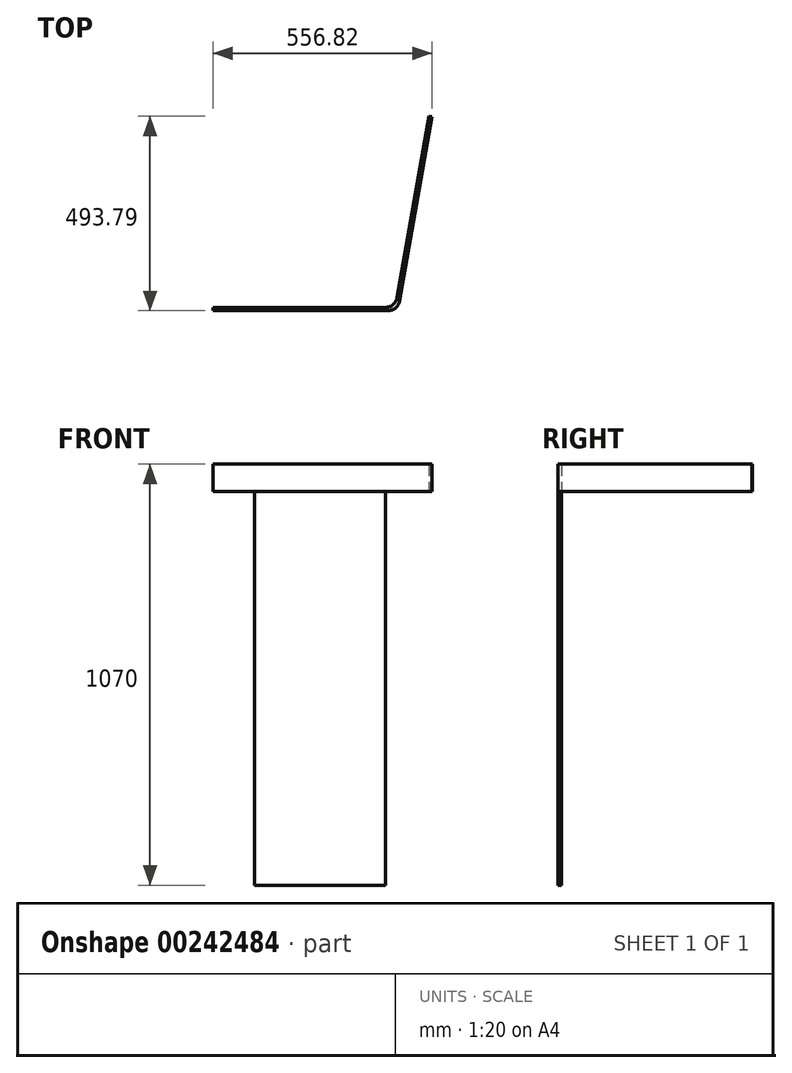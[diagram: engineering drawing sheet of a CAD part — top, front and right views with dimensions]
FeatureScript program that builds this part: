
annotation { "Feature Type Name" : "Feature", "Feature Type Description" : "" }
export const myFeature = defineFeature(function(context is Context, id is Id, definition is map)
    precondition{}
    {
        {
            var Q0;
            Q0=qCreatedBy(makeId("Top.planeOp"),FACE);
            var sketch = newSketch(context, id + "F0", { "sketchPlane" : qUnion([Q0])});
            skLineSegment(sketch, "E0", {"start": v(0, 0) * mm, "end": v(-470, 0) * mm});
            skLineSegment(sketch, "E1", {"start": v(0, 0) * mm, "end": v(86.82, 492.4) * mm});
            skLineSegment(sketch, "E2", {"start": v(-470, 0) * mm, "end": v(-470, 8) * mm});
            skLineSegment(sketch, "E3", {"start": v(-470, 8) * mm, "end": v(-6.71, 8) * mm});
            skLineSegment(sketch, "E4", {"start": v(86.82, 492.4) * mm, "end": v(78.95, 493.8) * mm});
            skLineSegment(sketch, "E5", {"start": v(78.95, 493.8) * mm, "end": v(-6.71, 8) * mm});
            skPoint(sketch, "E6.orphan", {"position": v(0, 8) * mm});
            skSolve(sketch);
        }
        {
            var Q0;
            Q0=makeQuery(id+"F0.imprint","IMPRINT",FACE,{"disambiguationData":[TD([[makeQuery(id+"F0.imprint","IMPRINT",EDGE,{"derivedFrom":sQuery(id+"F0.wireOp",EDGE,"E0")}),-1.0]])]});
            extrude(context, id + "F1", {"entities" : qUnion([Q0]), "depth" : 70 * mm});
        }
        {
            var Q0;
            Q0=makeQuery(id+"F1.opExtrude","SWEPT_EDGE",EDGE,{"disambiguationData":[OSD([sQuery(id+"F0.wireOp",EDGE,"E3"),sQuery(id+"F0.wireOp",EDGE,"E5")])]});
            var Q1;
            Q1=makeQuery(id+"F1.opExtrude","SWEPT_EDGE",EDGE,{"disambiguationData":[OSD([sQuery(id+"F0.wireOp",EDGE,"E0"),sQuery(id+"F0.wireOp",EDGE,"E1")])]});
            fillet(context, id + "F2", {"entities" : qUnion([Q0, Q1]), "radius" : 30 * mm, "tangentPropagation" : true, "allowEdgeOverflow" : false});
        }
        {
            var Q0;
            Q0=makeQuery(id+"F1.opExtrude","CAP_FACE",FACE,{"disambiguationData":[OSD([sQuery(id+"F0.wireOp",EDGE,"E0"),sQuery(id+"F0.wireOp",EDGE,"E1"),sQuery(id+"F0.wireOp",EDGE,"E2"),sQuery(id+"F0.wireOp",EDGE,"E3"),sQuery(id+"F0.wireOp",EDGE,"E4"),sQuery(id+"F0.wireOp",EDGE,"E5")])],"isStart":true});
            var sketch = newSketch(context, id + "F3", { "sketchPlane" : qUnion([Q0])});
            skLineSegment(sketch, "E7.bottom", {"start": v(-31.89, -8) * mm, "end": v(-364.15, -8) * mm});
            skLineSegment(sketch, "E7.top", {"start": v(-31.89, 0) * mm, "end": v(-364.15, 0) * mm});
            skLineSegment(sketch, "E7.left", {"start": v(-31.89, -8) * mm, "end": v(-31.89, 0) * mm});
            skLineSegment(sketch, "E7.right", {"start": v(-364.15, -8) * mm, "end": v(-364.15, 0) * mm});
            skSolve(sketch);
        }
        {
            var Q0;
            Q0=makeQuery(id+"F3.imprint","IMPRINT",FACE,{"disambiguationData":[TD([[makeQuery(id+"F3.imprint","IMPRINT",EDGE,{"derivedFrom":sQuery(id+"F3.wireOp",EDGE,"E7.bottom")}),1.0]])]});
            extrude(context, id + "F4", {"entities" : qUnion([Q0]), "depth" : 1000 * mm});
        }
    });
